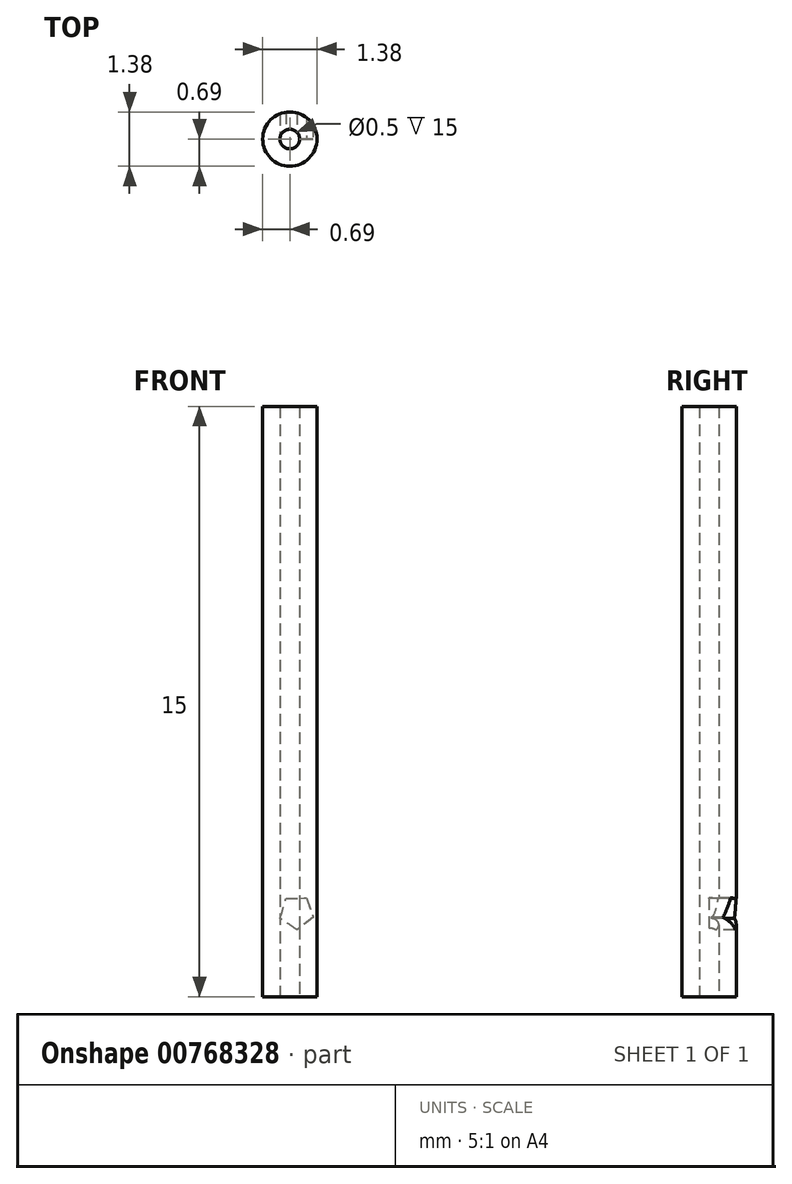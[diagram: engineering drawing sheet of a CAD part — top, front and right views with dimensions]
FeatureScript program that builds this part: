
annotation { "Feature Type Name" : "Feature", "Feature Type Description" : "" }
export const myFeature = defineFeature(function(context is Context, id is Id, definition is map)
    precondition{}
    {
        {
            var Q0;
            Q0=qCreatedBy(makeId("Top.planeOp"),FACE);
            var sketch = newSketch(context, id + "F0", { "sketchPlane" : qUnion([Q0])});
            skCircle(sketch, "E0", {"center": v(0, 0) * mm, "radius": 0.25 * mm});
            skCircle(sketch, "E1", {"center": v(0, 0) * mm, "radius": 0.7 * mm});
            skPoint(sketch, "E2", {"position": v(-0.18, 0.44) * mm});
            skCircle(sketch, "E3.cCircle", {"center": v(-0.18, 0.44) * mm, "radius": 0.27 * mm, "construction": true});
            skLineSegment(sketch, "E3.0", {"start": v(0.12, 0.58) * mm, "end": v(0.05, 0.2) * mm});
            skLineSegment(sketch, "E3.1", {"start": v(0.05, 0.2) * mm, "end": v(-0.34, 0.14) * mm});
            skLineSegment(sketch, "E3.2", {"start": v(-0.34, 0.14) * mm, "end": v(-0.5, 0.5) * mm});
            skLineSegment(sketch, "E3.3", {"start": v(-0.5, 0.5) * mm, "end": v(-0.22, 0.76) * mm});
            skLineSegment(sketch, "E3.4", {"start": v(-0.22, 0.76) * mm, "end": v(0.12, 0.58) * mm});
            skPoint(sketch, "E3.0.midPoint", {"position": v(0.08, 0.39) * mm});
            skSolve(sketch);
        }
        {
            var Q0;
            Q0=makeQuery(id+"F0.imprint","IMPRINT",FACE,{"disambiguationData":[TD([[makeQuery(id+"F0.imprint","IMPRINT",EDGE,{"derivedFrom":sQuery(id+"F0.wireOp",EDGE,"E0")}),-1.0]])]});
            extrude(context, id + "F1", {"entities" : qUnion([Q0]), "depth" : 15 * mm, "offsetDistance" : 25 * mm});
        }
        {
            var Q0;
            Q0=qCreatedBy(makeId("Front.planeOp"),FACE);
            var sketch = newSketch(context, id + "F2", { "sketchPlane" : qUnion([Q0])});
            skPoint(sketch, "E4", {"position": v(0.17, 2.14) * mm});
            skCircle(sketch, "E5.cCircle", {"center": v(0.17, 2.14) * mm, "radius": 0.36 * mm, "construction": true});
            skLineSegment(sketch, "E5.0", {"start": v(0.6, 2.02) * mm, "end": v(0.18, 1.7) * mm});
            skLineSegment(sketch, "E5.1", {"start": v(0.18, 1.7) * mm, "end": v(-0.25, 2) * mm});
            skLineSegment(sketch, "E5.2", {"start": v(-0.25, 2) * mm, "end": v(-0.1, 2.5) * mm});
            skLineSegment(sketch, "E5.3", {"start": v(-0.1, 2.5) * mm, "end": v(0.42, 2.5) * mm});
            skLineSegment(sketch, "E5.4", {"start": v(0.42, 2.5) * mm, "end": v(0.6, 2.02) * mm});
            skPoint(sketch, "E5.0.midPoint", {"position": v(0.39, 1.86) * mm});
            skSolve(sketch);
        }
        {
            var Q0;
            Q0 = qSketchRegion(id + "F2", true);
            extrude(context, id + "F3", {"entities" : qUnion([Q0]), "operationType" : NewBodyOperationType.REMOVE, "oppositeDirection" : true, "depth" : 0.7 * mm, "offsetDistance" : 25 * mm});
        }
    });
